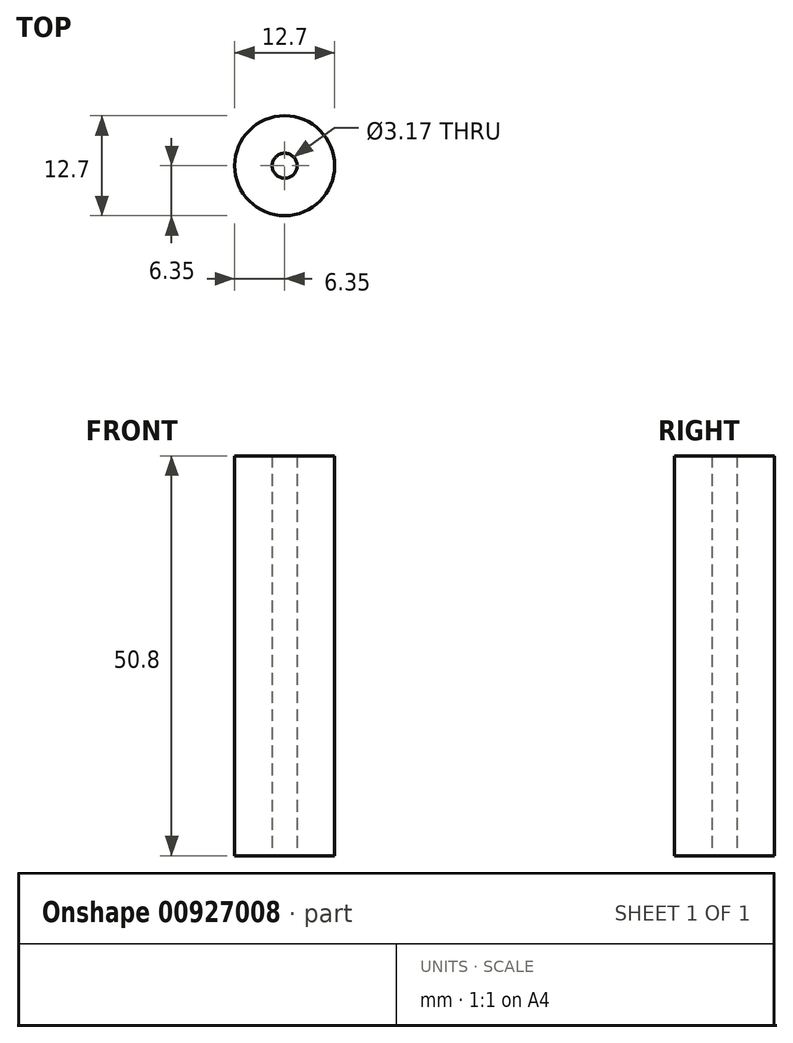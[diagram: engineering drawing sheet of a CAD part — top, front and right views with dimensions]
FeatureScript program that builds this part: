
annotation { "Feature Type Name" : "Feature", "Feature Type Description" : "" }
export const myFeature = defineFeature(function(context is Context, id is Id, definition is map)
    precondition{}
    {
        {
            var Q0;
            Q0=qCreatedBy(makeId("Top.planeOp"),FACE);
            var sketch = newSketch(context, id + "F0", { "sketchPlane" : qUnion([Q0])});
            skCircle(sketch, "E0", {"center": v(0, 0) * mm, "radius": 6.35 * mm});
            skCircle(sketch, "E1", {"center": v(0, 0) * mm, "radius": 1.59 * mm});
            skSolve(sketch);
        }
        {
            var Q0;
            Q0=makeQuery(id+"F0.imprint","IMPRINT",FACE,{"disambiguationData":[TD([[makeQuery(id+"F0.imprint","IMPRINT",EDGE,{"derivedFrom":sQuery(id+"F0.wireOp",EDGE,"E0")}),1.0]])]});
            extrude(context, id + "F1", {"entities" : qUnion([Q0]), "depth" : 50.8 * mm, "offsetDistance" : 25.4 * mm});
        }
    });
